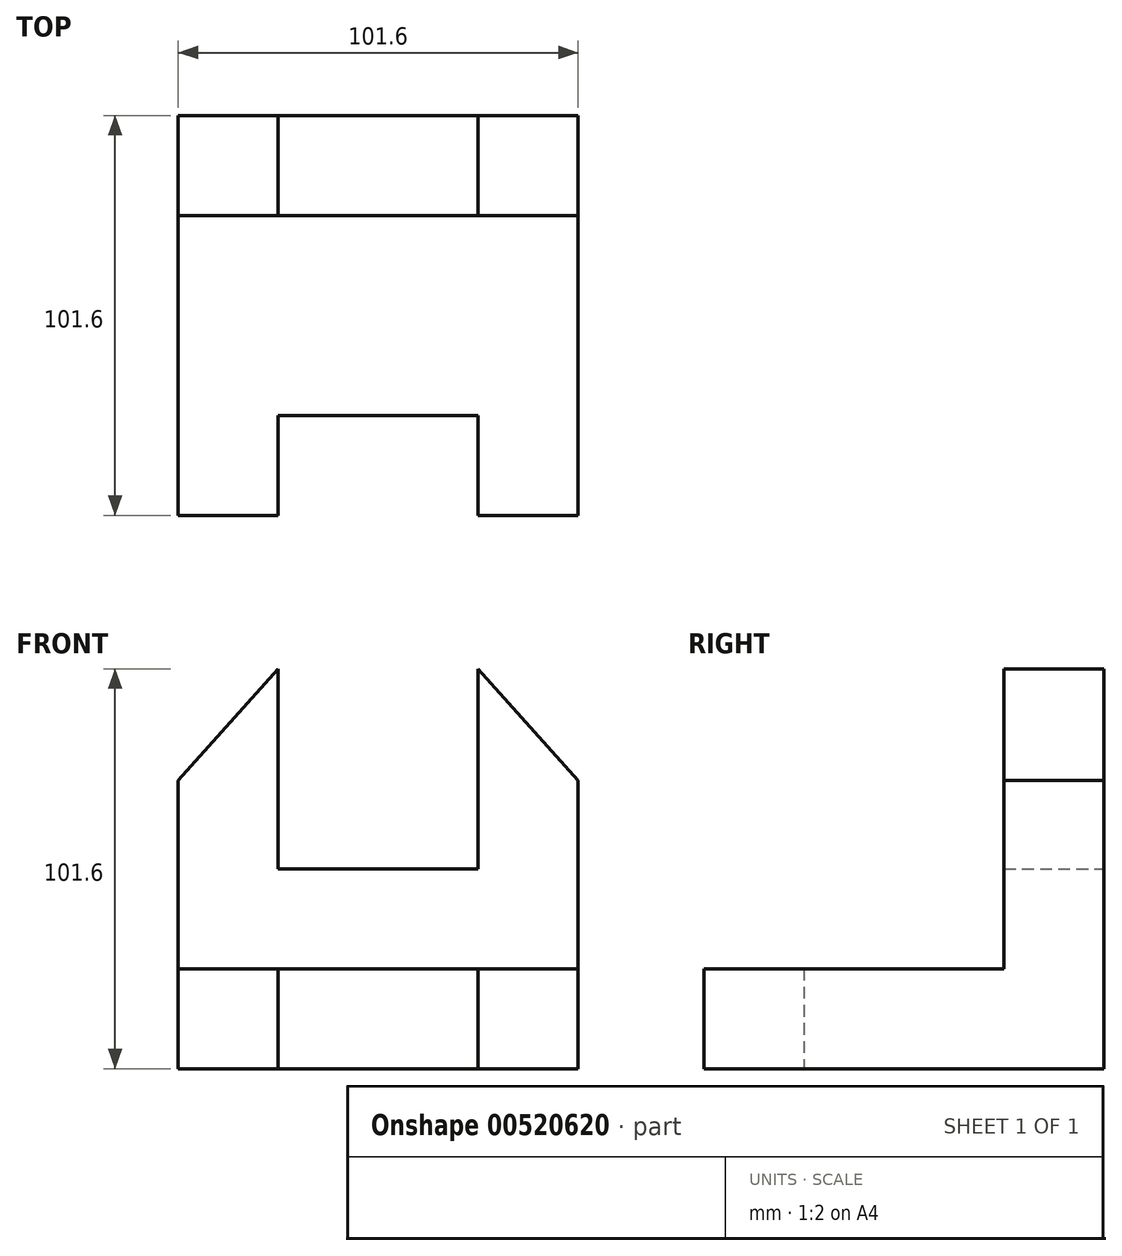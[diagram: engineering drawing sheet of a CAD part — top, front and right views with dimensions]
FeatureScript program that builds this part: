
annotation { "Feature Type Name" : "Feature", "Feature Type Description" : "" }
export const myFeature = defineFeature(function(context is Context, id is Id, definition is map)
    precondition{}
    {
        {
            var Q0;
            Q0=qCreatedBy(makeId("Front.planeOp"),FACE);
            var sketch = newSketch(context, id + "F0", { "sketchPlane" : qUnion([Q0])});
            skLineSegment(sketch, "E0", {"start": v(0, 0) * mm, "end": v(0, 101.6) * mm});
            skLineSegment(sketch, "E1", {"start": v(0, 101.6) * mm, "end": v(-25.4, 101.6) * mm});
            skLineSegment(sketch, "E2", {"start": v(-25.4, 101.6) * mm, "end": v(-25.4, 50.8) * mm});
            skLineSegment(sketch, "E3", {"start": v(-25.4, 50.8) * mm, "end": v(-76.2, 50.8) * mm});
            skLineSegment(sketch, "E4", {"start": v(-76.2, 50.8) * mm, "end": v(-76.2, 101.6) * mm});
            skLineSegment(sketch, "E5", {"start": v(-76.2, 101.6) * mm, "end": v(-101.6, 101.6) * mm});
            skLineSegment(sketch, "E6", {"start": v(-101.6, 101.6) * mm, "end": v(-101.6, 0) * mm});
            skLineSegment(sketch, "E7", {"start": v(-101.6, 0) * mm, "end": v(0, 0) * mm});
            skSolve(sketch);
        }
        {
            var Q0;
            Q0=makeQuery(id+"F0.imprint","IMPRINT",FACE,{"disambiguationData":[TD([[makeQuery(id+"F0.imprint","IMPRINT",EDGE,{"derivedFrom":sQuery(id+"F0.wireOp",EDGE,"E0")}),1.0]])]});
            extrude(context, id + "F1", {"entities" : qUnion([Q0]), "depth" : 25.4 * mm, "offsetDistance" : 25.4 * mm});
        }
        {
            var Q0;
            Q0=qCreatedBy(makeId("Right.planeOp"),FACE);
            var sketch = newSketch(context, id + "F2", { "sketchPlane" : qUnion([Q0])});
            skLineSegment(sketch, "E8", {"start": v(0, 0) * mm, "end": v(-76.2, 0) * mm});
            skLineSegment(sketch, "E9", {"start": v(-76.2, 0) * mm, "end": v(-76.2, 25.4) * mm});
            skLineSegment(sketch, "E10", {"start": v(-76.2, 25.4) * mm, "end": v(0, 25.4) * mm});
            skLineSegment(sketch, "E11", {"start": v(0, 25.4) * mm, "end": v(0, 0) * mm});
            skSolve(sketch);
        }
        {
            var Q0;
            Q0=makeQuery(id+"F2.imprint","IMPRINT",FACE,{"disambiguationData":[TD([[makeQuery(id+"F2.imprint","IMPRINT",EDGE,{"derivedFrom":sQuery(id+"F2.wireOp",EDGE,"E8")}),-1.0]])]});
            extrude(context, id + "F3", {"entities" : qUnion([Q0]), "operationType" : NewBodyOperationType.ADD, "oppositeDirection" : true, "depth" : 101.6 * mm, "offsetDistance" : 25.4 * mm});
        }
        {
            var Q0;
            Q0=makeQuery(id+"F3.opExtrude","SWEPT_FACE",FACE,{"disambiguationData":[OSD([sQuery(id+"F2.wireOp",EDGE,"E9")])]});
            var sketch = newSketch(context, id + "F4", { "sketchPlane" : qUnion([Q0])});
            skLineSegment(sketch, "E12.bottom", {"start": v(-101.6, 25.4) * mm, "end": v(-76.2, 25.4) * mm});
            skLineSegment(sketch, "E12.top", {"start": v(-101.6, 0) * mm, "end": v(-76.2, 0) * mm});
            skLineSegment(sketch, "E12.left", {"start": v(-101.6, 25.4) * mm, "end": v(-101.6, 0) * mm});
            skLineSegment(sketch, "E12.right", {"start": v(-76.2, 25.4) * mm, "end": v(-76.2, 0) * mm});
            skLineSegment(sketch, "E13.bottom", {"start": v(0, 25.4) * mm, "end": v(-25.4, 25.4) * mm});
            skLineSegment(sketch, "E13.top", {"start": v(0, 0) * mm, "end": v(-25.4, 0) * mm});
            skLineSegment(sketch, "E13.left", {"start": v(0, 25.4) * mm, "end": v(0, 0) * mm});
            skLineSegment(sketch, "E13.right", {"start": v(-25.4, 25.4) * mm, "end": v(-25.4, 0) * mm});
            skLineSegment(sketch, "E14.bottom", {"start": v(-76.2, 25.4) * mm, "end": v(-25.4, 25.4) * mm});
            skLineSegment(sketch, "E14.top", {"start": v(-76.2, 0) * mm, "end": v(-25.4, 0) * mm});
            skSolve(sketch);
        }
        {
            var Q0;
            Q0=makeQuery(id+"F4.imprint","IMPRINT",FACE,{"disambiguationData":[TD([[makeQuery(id+"F4.imprint","IMPRINT",EDGE,{"derivedFrom":sQuery(id+"F4.wireOp",EDGE,"E14.bottom")}),-1.0]])]});
            extrude(context, id + "F5", {"entities" : qUnion([Q0]), "operationType" : NewBodyOperationType.REMOVE, "oppositeDirection" : true, "depth" : 25.4 * mm, "offsetDistance" : 25.4 * mm});
        }
        {
            var Q0;
            Q0=makeQuery(id+"F1.opExtrude","CAP_FACE",FACE,{"disambiguationData":[OSD([sQuery(id+"F0.wireOp",EDGE,"E0"),sQuery(id+"F0.wireOp",EDGE,"E1"),sQuery(id+"F0.wireOp",EDGE,"E2"),sQuery(id+"F0.wireOp",EDGE,"E3"),sQuery(id+"F0.wireOp",EDGE,"E4"),sQuery(id+"F0.wireOp",EDGE,"E5"),sQuery(id+"F0.wireOp",EDGE,"E6"),sQuery(id+"F0.wireOp",EDGE,"E7")])],"isStart":false});
            var sketch = newSketch(context, id + "F6", { "sketchPlane" : qUnion([Q0])});
            skLineSegment(sketch, "E15", {"start": v(-25.4, 101.6) * mm, "end": v(0, 73.2) * mm});
            skLineSegment(sketch, "E16", {"start": v(0, 73.2) * mm, "end": v(0, 101.6) * mm});
            skLineSegment(sketch, "E17", {"start": v(0, 101.6) * mm, "end": v(-25.4, 101.6) * mm});
            skSolve(sketch);
        }
        {
            var Q0;
            Q0=makeQuery(id+"F6.imprint","IMPRINT",FACE,{"disambiguationData":[TD([[makeQuery(id+"F6.imprint","IMPRINT",EDGE,{"derivedFrom":sQuery(id+"F6.wireOp",EDGE,"E15")}),1.0]])]});
            extrude(context, id + "F7", {"entities" : qUnion([Q0]), "operationType" : NewBodyOperationType.REMOVE, "oppositeDirection" : true, "depth" : 25.4 * mm, "offsetDistance" : 25.4 * mm});
        }
        {
            var Q0;
            Q0=makeQuery(id+"F1.opExtrude","CAP_FACE",FACE,{"disambiguationData":[OSD([sQuery(id+"F0.wireOp",EDGE,"E0"),sQuery(id+"F0.wireOp",EDGE,"E1"),sQuery(id+"F0.wireOp",EDGE,"E2"),sQuery(id+"F0.wireOp",EDGE,"E3"),sQuery(id+"F0.wireOp",EDGE,"E4"),sQuery(id+"F0.wireOp",EDGE,"E5"),sQuery(id+"F0.wireOp",EDGE,"E6"),sQuery(id+"F0.wireOp",EDGE,"E7")])],"isStart":false});
            var sketch = newSketch(context, id + "F8", { "sketchPlane" : qUnion([Q0])});
            skLineSegment(sketch, "E18", {"start": v(-76.2, 101.6) * mm, "end": v(-101.6, 73.2) * mm});
            skLineSegment(sketch, "E19", {"start": v(-101.6, 73.2) * mm, "end": v(-101.6, 101.6) * mm});
            skLineSegment(sketch, "E20", {"start": v(-101.6, 101.6) * mm, "end": v(-76.2, 101.6) * mm});
            skSolve(sketch);
        }
        {
            var Q0;
            Q0=makeQuery(id+"F8.imprint","IMPRINT",FACE,{"disambiguationData":[TD([[makeQuery(id+"F8.imprint","IMPRINT",EDGE,{"derivedFrom":sQuery(id+"F8.wireOp",EDGE,"E18")}),-1.0]])]});
            extrude(context, id + "F9", {"entities" : qUnion([Q0]), "operationType" : NewBodyOperationType.REMOVE, "oppositeDirection" : true, "depth" : 25.4 * mm, "offsetDistance" : 25.4 * mm});
        }
        {
            var Q0;
            {var subQ2=sQuery(id+"F2.wireOp",EDGE,"E9");Q0=makeQuery(id+"F5.boolean.opBoolean","SPLIT",FACE,{"disambiguationData":[TD([makeQuery(id+"F1.opExtrude","SWEPT_FACE",FACE,{"disambiguationData":[OSD([sQuery(id+"F0.wireOp",EDGE,"E0")])]})])],"derivedFrom":makeQuery(id+"F3.opExtrude","SWEPT_FACE",FACE,{"disambiguationData":[OSD([subQ2])]})});}
            extrude(context, id + "F10", {"entities" : qUnion([Q0]), "operationType" : NewBodyOperationType.ADD, "depth" : 25.4 * mm, "offsetDistance" : 25.4 * mm});
        }
        {
            var Q0;
            {var subQ1=sQuery(id+"F2.wireOp",EDGE,"E9");Q0=makeQuery(id+"F5.boolean.opBoolean","SPLIT",FACE,{"disambiguationData":[TD([makeQuery(id+"F1.opExtrude","SWEPT_FACE",FACE,{"disambiguationData":[OSD([sQuery(id+"F0.wireOp",EDGE,"E6")])]})])],"derivedFrom":makeQuery(id+"F3.opExtrude","SWEPT_FACE",FACE,{"disambiguationData":[OSD([subQ1])]})});}
            extrude(context, id + "F11", {"entities" : qUnion([Q0]), "operationType" : NewBodyOperationType.ADD, "depth" : 25.4 * mm, "offsetDistance" : 25.4 * mm});
        }
        {
            var Q0;
            Q0=makeQuery(id+"F5.boolean.opBoolean","COPY",FACE,{"derivedFrom":makeQuery(id+"F5.opExtrude","CAP_FACE",FACE,{"disambiguationData":[OSD([sQuery(id+"F4.wireOp",EDGE,"E14.bottom"),sQuery(id+"F4.wireOp",EDGE,"E14.top"),sQuery(id+"F4.wireOp",EDGE,"E12.right"),sQuery(id+"F4.wireOp",EDGE,"E13.right")])],"isStart":false})});
            extrude(context, id + "F12", {"entities" : qUnion([Q0]), "operationType" : NewBodyOperationType.ADD, "depth" : 25.4 * mm, "offsetDistance" : 25.4 * mm});
        }
    });
